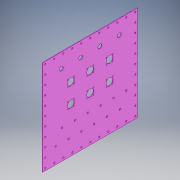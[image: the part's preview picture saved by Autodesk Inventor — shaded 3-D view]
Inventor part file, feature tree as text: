
AUTODESK INVENTOR PART (.ipt)
format: ipt  version: 2017 (Build 210142000, 142)  size: 322,048 bytes
history: native  units: in
note: dims shown in document units (in); Inventor stores cm internally (conversion verified against a paired STEP export)
features: other x8, extrude x3, hole x1, sketch x1
ambient origin geometry x8: Origin, YZ Plane, XZ Plane, XY Plane, X Axis, Y Axis, Z Axis, Center Point
bodies: Solid1 (feature_tree)
feature tree (13):
  other  "sma"
  other  "rj45"
  extrude  "Extrusion1"  Depth=0.3937in
  extrude  "Extrusion3"  Depth=0.3937in
  hole  "Hole1"  [1 undecoded]
  extrude  "Extrusion5"  Depth=3.0in
  sketch  "Sketch5"  dims[d14=2.3622in d16=0.3937in d28=1.1024in d29=1.378in d34=4.362in d36=1.1811in d38=3.0in d39=0.7874in d41=3.0in d44=2.5in d45=0.625in d46=2.5in d47=1.5748in d49=3.0in d50=0.3937in d52=0.3937in d54=2.862in d55=0.0in d56=0.0in d59=0.0in d60=0.0in d61=0.134in d62=0.2362in d63=0.119in d64=0.25in d65=0.563in d66=0.3465in d67=0.8108in d70=45.0deg d71=45.0deg d76=0.253in d79=1.9685in d80=0.113in d81=2.5in d82=0.253in d83=0.113in d84=1.0in d85=2.0in d86=2.3622in d88=2.0in d89=0.3937in d91=0.3937in d93=0.0in d94=0.0in d95=45.0deg d96=45.0deg d97=45.0deg d98=45.0deg d99=45.0deg d100=45.0deg d101=45.0deg d102=45.0deg]
  other  "Work Axis1"
  other  "Work Axis2"
  other  "Work Axis3"
  other  "Work Axis4"
  other  "waveguide"
  other  "RD-A001-P001-REV0"
note: 1 required parameter value undecoded (feature->parameter linkage not recoverable at this tier; creation-order binding heuristic only, values carry confidence <= 0.55)
